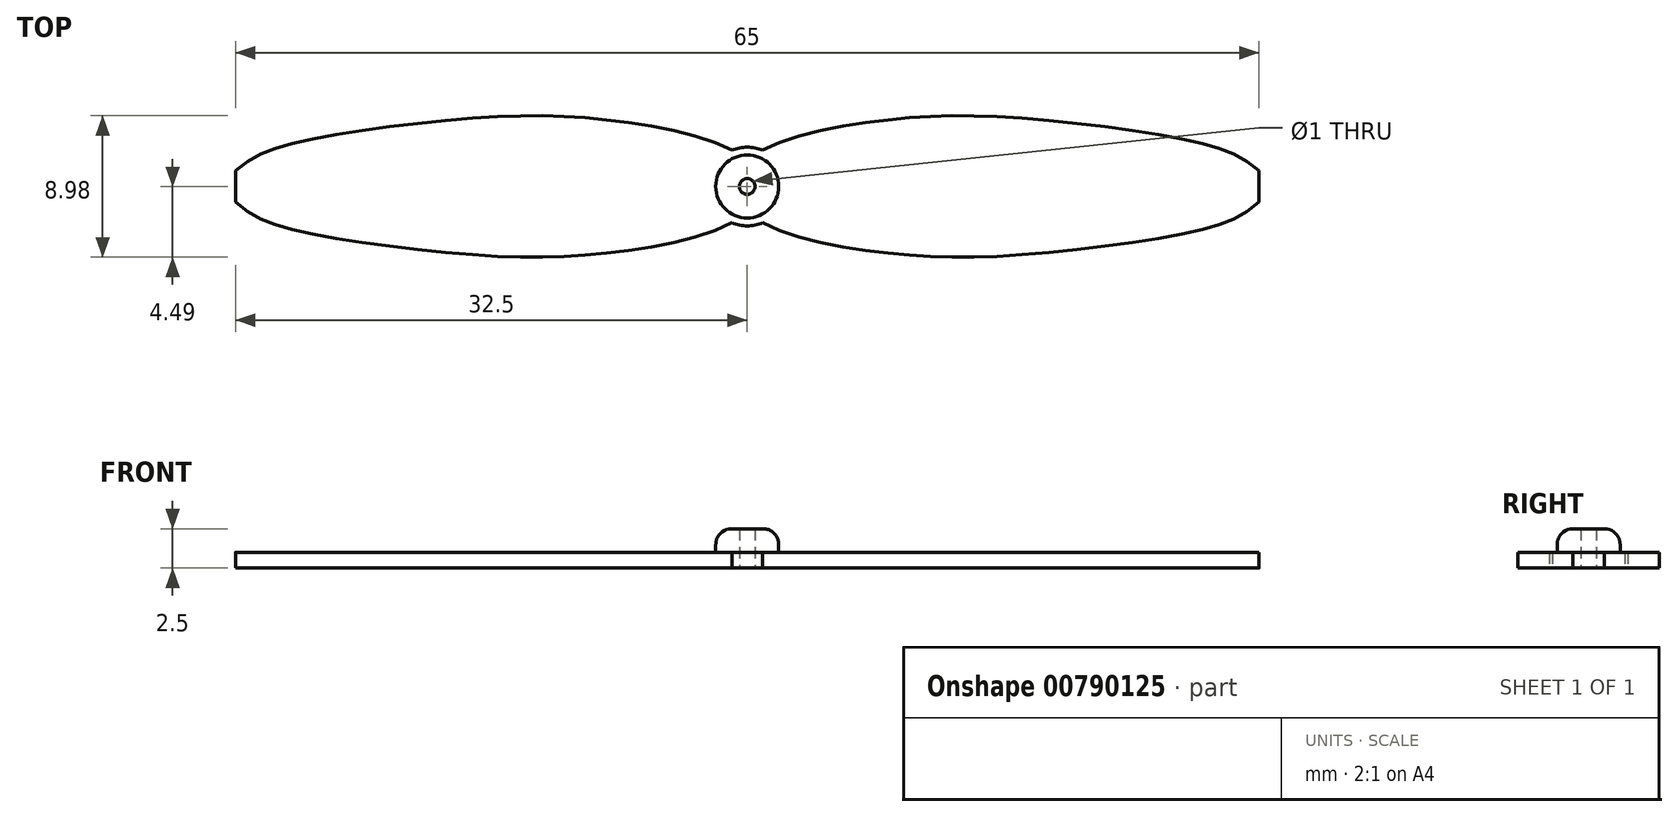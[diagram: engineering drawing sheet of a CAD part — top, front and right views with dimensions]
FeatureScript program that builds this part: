
annotation { "Feature Type Name" : "Feature", "Feature Type Description" : "" }
export const myFeature = defineFeature(function(context is Context, id is Id, definition is map)
    precondition{}
    {
        {
            var Q0;
            Q0=qCreatedBy(makeId("Top.planeOp"),FACE);
            var sketch = newSketch(context, id + "F0", { "sketchPlane" : qUnion([Q0])});
            skArc(sketch, "E0", {"start": v(-0.98, -2.3) * mm, "mid": v(0, -2.5) * mm, "end": v(0.98, -2.3) * mm});
            skCircle(sketch, "E1", {"center": v(0, 0) * mm, "radius": 0.5 * mm});
            skArc(sketch, "E2", {"start": v(-32.48, 1) * mm, "mid": v(-32.5, 0) * mm, "end": v(-32.48, -1) * mm});
            skArc(sketch, "E3.trimOffspring", {"start": v(0.98, 2.3) * mm, "mid": v(0, 2.5) * mm, "end": v(-0.98, 2.3) * mm});
            skArc(sketch, "E4.trimOffspring", {"start": v(32.48, -1) * mm, "mid": v(32.5, 0) * mm, "end": v(32.48, 1) * mm});
            skFitSpline(sketch, "E5", {"points": [v(-0.98, 2.3) * mm, v(-8.6, 4.2) * mm, v(-17, 4.37) * mm, v(-28.6, 2.8) * mm, v(-32.48, 1) * mm], "startDerivative": vector(-22.63, 12.2) * mm, "endDerivative": vector(-17.46, -15.57) * mm});
            skFitSpline(sketch, "E6.MirrorCS", {"points": [v(-0.98, -2.3) * mm, v(-8.6, -4.2) * mm, v(-17, -4.37) * mm, v(-28.6, -2.8) * mm, v(-32.48, -1) * mm], "startDerivative": vector(-22.63, -12.2) * mm, "endDerivative": vector(-17.46, 15.57) * mm});
            skFitSpline(sketch, "E7.MirrorCS", {"points": [v(0.98, 2.3) * mm, v(8.6, 4.2) * mm, v(17, 4.37) * mm, v(28.6, 2.8) * mm, v(32.48, 1) * mm], "startDerivative": vector(22.63, 12.2) * mm, "endDerivative": vector(17.46, -15.57) * mm});
            skFitSpline(sketch, "E8.MirrorCS", {"points": [v(0.98, -2.3) * mm, v(8.6, -4.2) * mm, v(17, -4.37) * mm, v(28.6, -2.8) * mm, v(32.48, -1) * mm], "startDerivative": vector(22.63, -12.2) * mm, "endDerivative": vector(17.46, 15.57) * mm});
            skSolve(sketch);
        }
        {
            var Q0;
            Q0=makeQuery(id+"F0.imprint","IMPRINT",FACE,{"disambiguationData":[TD([[makeQuery(id+"F0.imprint","IMPRINT",EDGE,{"derivedFrom":sQuery(id+"F0.wireOp",EDGE,"E0")}),1.0]])]});
            extrude(context, id + "F1", {"entities" : qUnion([Q0]), "depth" : 1 * mm});
        }
        {
            var Q0;
            Q0=makeQuery(id+"F1.opExtrude","CAP_FACE",FACE,{"disambiguationData":[OSD([sQuery(id+"F0.wireOp",EDGE,"E0"),sQuery(id+"F0.wireOp",EDGE,"E1"),sQuery(id+"F0.wireOp",EDGE,"E2"),sQuery(id+"F0.wireOp",EDGE,"E3.trimOffspring"),sQuery(id+"F0.wireOp",EDGE,"E4.trimOffspring"),sQuery(id+"F0.wireOp",EDGE,"E5"),sQuery(id+"F0.wireOp",EDGE,"E6.MirrorCS"),sQuery(id+"F0.wireOp",EDGE,"E7.MirrorCS"),sQuery(id+"F0.wireOp",EDGE,"E8.MirrorCS")])],"isStart":false});
            var sketch = newSketch(context, id + "F2", { "sketchPlane" : qUnion([Q0])});
            skCircle(sketch, "E9", {"center": v(0, 0) * mm, "radius": 2 * mm});
            skCircle(sketch, "E10", {"center": v(0, 0) * mm, "radius": 0.5 * mm});
            skSolve(sketch);
        }
        {
            var Q0;
            Q0=makeQuery(id+"F2.imprint","IMPRINT",FACE,{"disambiguationData":[TD([[makeQuery(id+"F2.imprint","IMPRINT",EDGE,{"derivedFrom":sQuery(id+"F2.wireOp",EDGE,"E9")}),1.0]])]});
            extrude(context, id + "F3", {"entities" : qUnion([Q0]), "operationType" : NewBodyOperationType.ADD, "depth" : 1.5 * mm, "offsetDistance" : 25 * mm});
        }
        {
            var Q0;
            Q0=makeQuery(id+"F3.opExtrude","CAP_EDGE",EDGE,{"disambiguationData":[OSD([sQuery(id+"F2.wireOp",EDGE,"E9")])],"isStart":false});
            fillet(context, id + "F4", {"entities" : qUnion([Q0]), "radius" : 1 * mm, "tangentPropagation" : true, "allowEdgeOverflow" : false});
        }
    });
